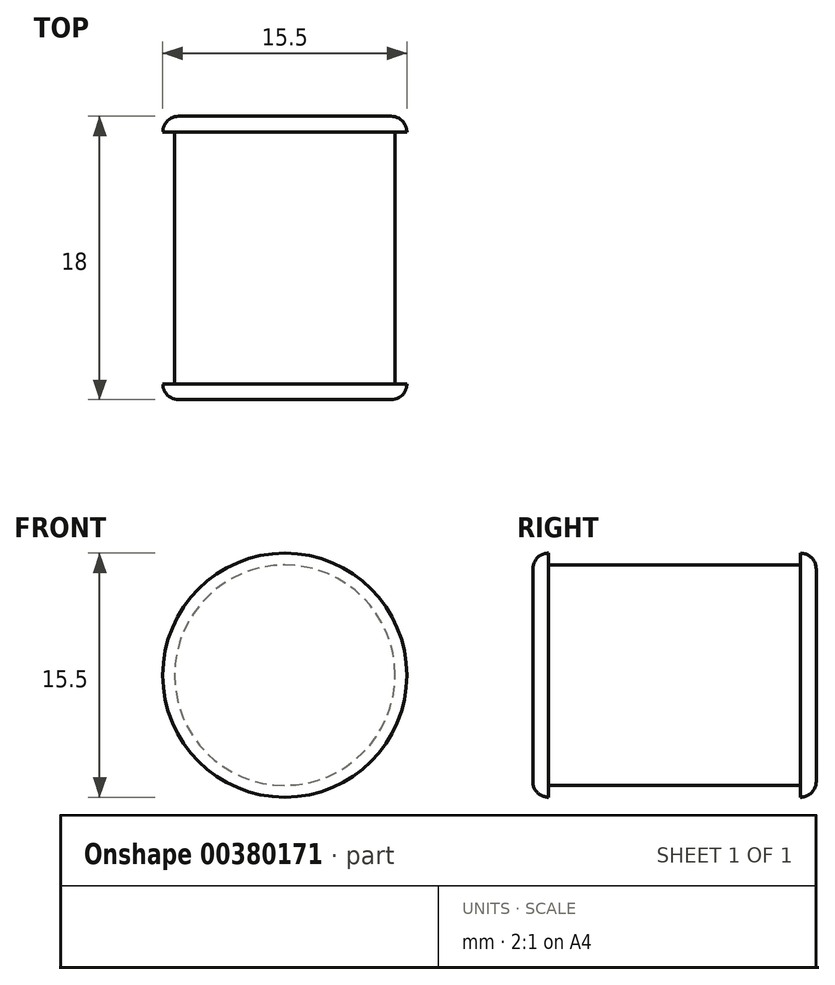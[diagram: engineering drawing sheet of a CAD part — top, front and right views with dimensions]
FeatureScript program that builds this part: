
annotation { "Feature Type Name" : "Feature", "Feature Type Description" : "" }
export const myFeature = defineFeature(function(context is Context, id is Id, definition is map)
    precondition{}
    {
        {
            var Q0;
            Q0=qCreatedBy(makeId("Front.planeOp"),FACE);
            var sketch = newSketch(context, id + "F0", { "sketchPlane" : qUnion([Q0])});
            skCircle(sketch, "E0", {"center": v(0, 0) * mm, "radius": 7 * mm});
            skSolve(sketch);
        }
        {
            var Q0;
            Q0=makeQuery(id+"F0.imprint","IMPRINT",FACE,{"disambiguationData":[TD([[makeQuery(id+"F0.imprint","IMPRINT",EDGE,{"derivedFrom":sQuery(id+"F0.wireOp",EDGE,"E0")}),1.0]])]});
            extrude(context, id + "F1", {"entities" : qUnion([Q0]), "endBound" : BoundingType.SYMMETRIC, "depth" : 16 * mm});
        }
        {
            var Q0;
            Q0=makeQuery(id+"F1.opExtrude","CAP_FACE",FACE,{"disambiguationData":[OSD([sQuery(id+"F0.wireOp",EDGE,"E0")])],"isStart":false});
            var sketch = newSketch(context, id + "F2", { "sketchPlane" : qUnion([Q0])});
            skCircle(sketch, "E1", {"center": v(0, 0) * mm, "radius": 7.75 * mm});
            skSolve(sketch);
        }
        {
            var Q0;
            Q0=makeQuery(id+"F2.imprint","IMPRINT",FACE,{"disambiguationData":[TD([[makeQuery(id+"F2.imprint","IMPRINT",EDGE,{"derivedFrom":sQuery(id+"F2.wireOp",EDGE,"E1")}),1.0]])]});
            var Q1;
            Q1=makeQuery(id+"F2.imprint","IMPRINT",FACE,{"disambiguationData":[TD([[makeQuery(id+"F2.imprint","IMPRINT",EDGE,{"derivedFrom":makeQuery(id+"F1.opExtrude","CAP_EDGE",EDGE,{"disambiguationData":[OSD([sQuery(id+"F0.wireOp",EDGE,"E0")])],"isStart":false})}),1.0]])]});
            extrude(context, id + "F3", {"entities" : qUnion([Q0, Q1]), "operationType" : NewBodyOperationType.ADD, "depth" : 1 * mm});
        }
        {
            var Q0;
            Q0=makeQuery(id+"F1.opExtrude","CAP_FACE",FACE,{"disambiguationData":[OSD([sQuery(id+"F0.wireOp",EDGE,"E0")])],"isStart":true});
            var sketch = newSketch(context, id + "F4", { "sketchPlane" : qUnion([Q0])});
            skCircle(sketch, "E2", {"center": v(0, 0) * mm, "radius": 7.75 * mm});
            skSolve(sketch);
        }
        {
            var Q0;
            Q0=makeQuery(id+"F4.imprint","IMPRINT",FACE,{"disambiguationData":[TD([[makeQuery(id+"F4.imprint","IMPRINT",EDGE,{"derivedFrom":makeQuery(id+"F1.opExtrude","CAP_EDGE",EDGE,{"disambiguationData":[OSD([sQuery(id+"F0.wireOp",EDGE,"E0")])],"isStart":true})}),-1.0]])]});
            var Q1;
            Q1=makeQuery(id+"F4.imprint","IMPRINT",FACE,{"disambiguationData":[TD([[makeQuery(id+"F4.imprint","IMPRINT",EDGE,{"derivedFrom":sQuery(id+"F4.wireOp",EDGE,"E2")}),1.0]])]});
            extrude(context, id + "F5", {"entities" : qUnion([Q0, Q1]), "operationType" : NewBodyOperationType.ADD, "depth" : 1 * mm});
        }
        {
            var Q0;
            Q0=makeQuery(id+"F3.opExtrude","CAP_EDGE",EDGE,{"disambiguationData":[OSD([sQuery(id+"F2.wireOp",EDGE,"E1")])],"isStart":false});
            var Q1;
            Q1=makeQuery(id+"F5.opExtrude","CAP_EDGE",EDGE,{"disambiguationData":[OSD([sQuery(id+"F4.wireOp",EDGE,"E2")])],"isStart":false});
            fillet(context, id + "F6", {"entities" : qUnion([Q0, Q1]), "radius" : 1 * mm, "tangentPropagation" : true, "allowEdgeOverflow" : false});
        }
    });
